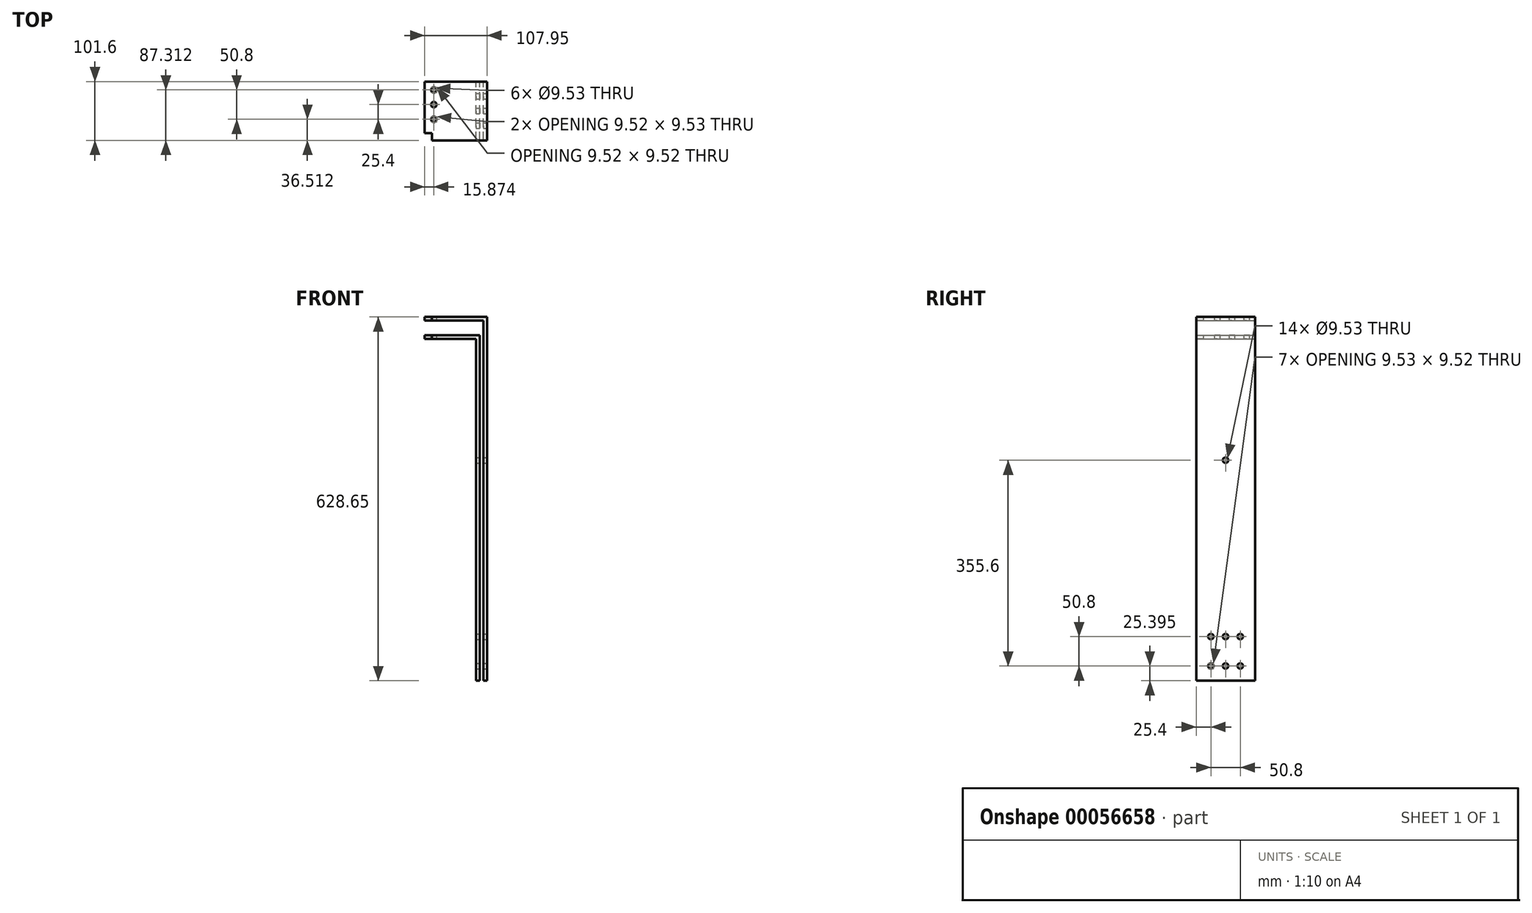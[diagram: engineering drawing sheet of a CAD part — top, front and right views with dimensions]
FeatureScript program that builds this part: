
annotation { "Feature Type Name" : "Feature", "Feature Type Description" : "" }
export const myFeature = defineFeature(function(context is Context, id is Id, definition is map)
    precondition{}
    {
        {
            var Q0;
            Q0=qCreatedBy(makeId("Front.planeOp"),FACE);
            var sketch = newSketch(context, id + "F0", { "sketchPlane" : qUnion([Q0])});
            skLineSegment(sketch, "E0", {"start": v(-138.97, 109.27) * mm, "end": v(-43.72, 109.27) * mm});
            skLineSegment(sketch, "E1", {"start": v(-43.72, 109.27) * mm, "end": v(-43.72, -487.63) * mm});
            skLineSegment(sketch, "E2", {"start": v(-50.07, 102.92) * mm, "end": v(-138.97, 102.92) * mm});
            skLineSegment(sketch, "E3", {"start": v(-37.37, 134.67) * mm, "end": v(-138.97, 134.67) * mm});
            skLineSegment(sketch, "E4", {"start": v(-138.97, 134.67) * mm, "end": v(-138.97, 141.02) * mm});
            skLineSegment(sketch, "E5", {"start": v(-138.97, 141.02) * mm, "end": v(-31.02, 141.02) * mm});
            skLineSegment(sketch, "E6", {"start": v(-31.02, 141.02) * mm, "end": v(-31.02, -487.63) * mm});
            skLineSegment(sketch, "E7", {"start": v(-50.07, -487.63) * mm, "end": v(-43.72, -487.63) * mm});
            skLineSegment(sketch, "E8.trimOffspring", {"start": v(-50.07, -487.63) * mm, "end": v(-50.07, 102.92) * mm});
            skLineSegment(sketch, "E9.trimOffspring", {"start": v(-37.37, -487.63) * mm, "end": v(-37.37, 134.67) * mm});
            skLineSegment(sketch, "E10.trimOffspring", {"start": v(-37.37, -487.63) * mm, "end": v(-31.02, -487.63) * mm});
            skLineSegment(sketch, "E11", {"start": v(-138.97, 109.27) * mm, "end": v(-138.97, 102.92) * mm});
            skSolve(sketch);
        }
        {
            var Q0;
            Q0=qSketchRegion(id+"F0",true);
            extrude(context, id + "F1", {"entities" : qUnion([Q0]), "endBound" : BoundingType.SYMMETRIC, "depth" : 101.6 * mm});
        }
        {
            var Q0;
            Q0=makeQuery(id+"F1.opExtrude","SWEPT_FACE",FACE,{"disambiguationData":[OSD([sQuery(id+"F0.wireOp",EDGE,"E6")])]});
            var sketch = newSketch(context, id + "F2", { "sketchPlane" : qUnion([Q0])});
            skCircle(sketch, "E12", {"center": v(-25.4, -462.23) * mm, "radius": 4.76 * mm});
            skCircle(sketch, "E13.0.1.0", {"center": v(-25.4, -411.43) * mm, "radius": 4.76 * mm});
            skCircle(sketch, "E13.1.0.0", {"center": v(0, -462.23) * mm, "radius": 4.76 * mm});
            skCircle(sketch, "E13.1.1.0", {"center": v(0, -411.43) * mm, "radius": 4.76 * mm});
            skCircle(sketch, "E13.2.0.0", {"center": v(25.4, -462.23) * mm, "radius": 4.76 * mm});
            skCircle(sketch, "E13.2.1.0", {"center": v(25.4, -411.43) * mm, "radius": 4.76 * mm});
            skLineSegment(sketch, "E13.direction1", {"start": v(-25.4, -462.23) * mm, "end": v(0, -462.23) * mm, "construction": true});
            skLineSegment(sketch, "E13.direction2", {"start": v(-25.4, -462.23) * mm, "end": v(-25.4, -411.43) * mm, "construction": true});
            skCircle(sketch, "E14", {"center": v(0, -106.63) * mm, "radius": 4.76 * mm});
            skSolve(sketch);
        }
        {
            var Q0;
            Q0=qSketchRegion(id+"F2",true);
            extrude(context, id + "F3", {"entities" : qUnion([Q0]), "operationType" : NewBodyOperationType.REMOVE, "endBound" : BoundingType.THROUGH_ALL, "oppositeDirection" : true, "depth" : 25.4 * mm});
        }
        {
            var Q0;
            Q0=makeQuery(id+"F1.opExtrude","SWEPT_FACE",FACE,{"disambiguationData":[OSD([sQuery(id+"F0.wireOp",EDGE,"E5")])]});
            var sketch = newSketch(context, id + "F4", { "sketchPlane" : qUnion([Q0])});
            skCircle(sketch, "E15", {"center": v(-123.1, -14.29) * mm, "radius": 4.76 * mm});
            skCircle(sketch, "E16.0.1.0", {"center": v(-123.1, 11.11) * mm, "radius": 4.76 * mm});
            skCircle(sketch, "E16.0.2.0", {"center": v(-123.1, 36.51) * mm, "radius": 4.76 * mm});
            skLineSegment(sketch, "E16.direction1", {"start": v(-123.1, -14.29) * mm, "end": v(-97.7, -14.29) * mm, "construction": true});
            skLineSegment(sketch, "E16.direction2", {"start": v(-123.1, -14.29) * mm, "end": v(-123.1, 11.11) * mm, "construction": true});
            skLineSegment(sketch, "E17.bottom", {"start": v(-138.97, -50.8) * mm, "end": v(-126.27, -50.8) * mm});
            skLineSegment(sketch, "E17.top", {"start": v(-138.97, -38.1) * mm, "end": v(-126.27, -38.1) * mm});
            skLineSegment(sketch, "E17.left", {"start": v(-138.97, -50.8) * mm, "end": v(-138.97, -38.1) * mm});
            skLineSegment(sketch, "E17.right", {"start": v(-126.27, -50.8) * mm, "end": v(-126.27, -38.1) * mm});
            skSolve(sketch);
        }
        {
            var Q0;
            Q0=qSketchRegion(id+"F4",true);
            extrude(context, id + "F5", {"entities" : qUnion([Q0]), "operationType" : NewBodyOperationType.REMOVE, "endBound" : BoundingType.THROUGH_ALL, "oppositeDirection" : true, "depth" : 25.4 * mm});
        }
    });
